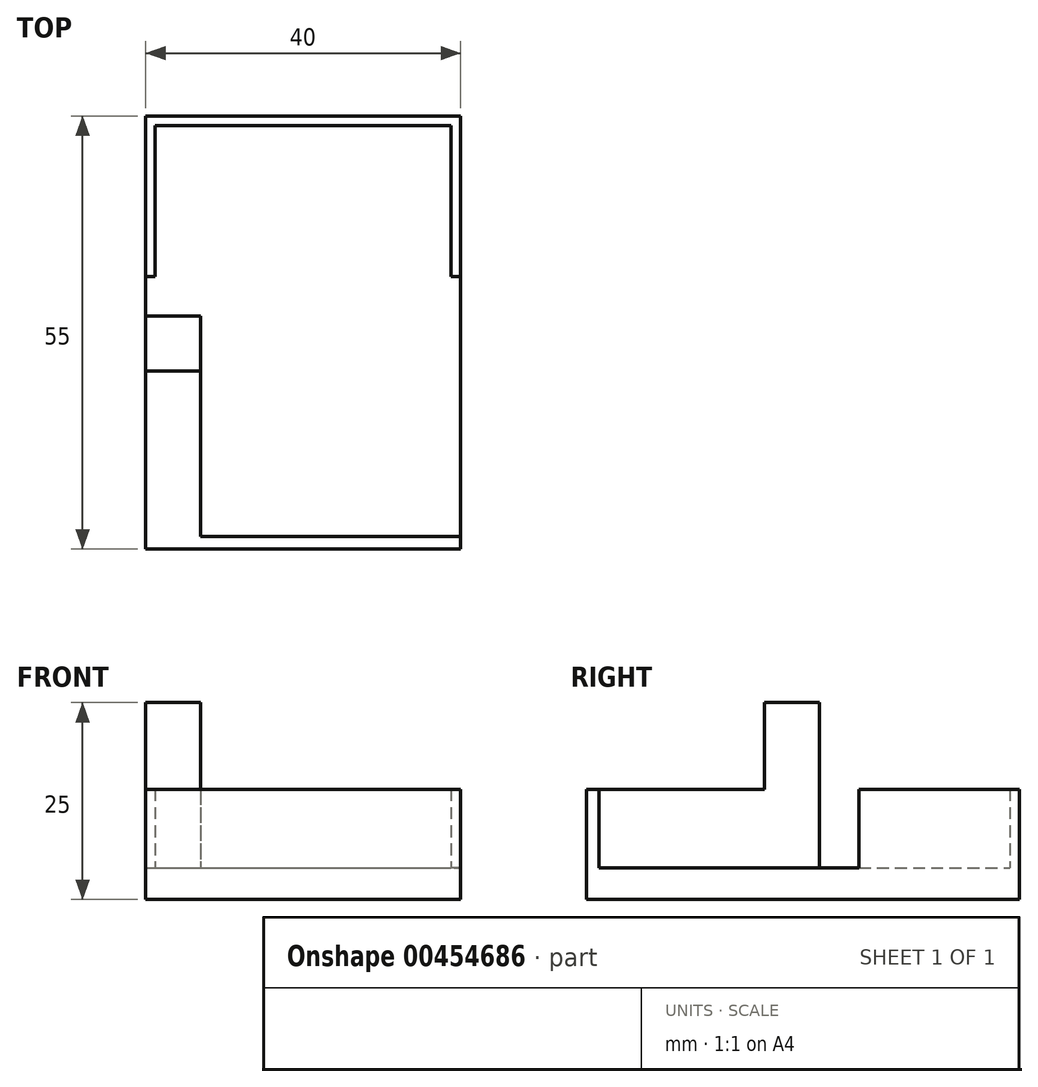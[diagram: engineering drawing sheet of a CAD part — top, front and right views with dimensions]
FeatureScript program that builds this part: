
annotation { "Feature Type Name" : "Feature", "Feature Type Description" : "" }
export const myFeature = defineFeature(function(context is Context, id is Id, definition is map)
    precondition{}
    {
        {
            var Q0;
            Q0=qCreatedBy(makeId("Top.planeOp"),FACE);
            var sketch = newSketch(context, id + "F0", { "sketchPlane" : qUnion([Q0])});
            skLineSegment(sketch, "E0.bottom", {"start": v(0, 0) * mm, "end": v(40, 0) * mm});
            skLineSegment(sketch, "E0.top", {"start": v(0, 55) * mm, "end": v(40, 55) * mm});
            skLineSegment(sketch, "E0.left", {"start": v(0, 0) * mm, "end": v(0, 55) * mm});
            skLineSegment(sketch, "E0.right", {"start": v(40, 0) * mm, "end": v(40, 55) * mm});
            skLineSegment(sketch, "E1.0", {"start": v(7, 1.6) * mm, "end": v(40, 1.6) * mm});
            skLineSegment(sketch, "E2.0", {"start": v(0, 29.6) * mm, "end": v(7, 29.6) * mm});
            skLineSegment(sketch, "E3.0", {"start": v(7, 1.6) * mm, "end": v(7, 29.6) * mm});
            skLineSegment(sketch, "E4.0", {"start": v(0, 34.6) * mm, "end": v(1.2, 34.6) * mm});
            skLineSegment(sketch, "E5.0", {"start": v(1.2, 53.8) * mm, "end": v(38.8, 53.8) * mm});
            skLineSegment(sketch, "E6", {"start": v(40, 34.6) * mm, "end": v(38.8, 34.6) * mm});
            skLineSegment(sketch, "E7", {"start": v(38.8, 34.6) * mm, "end": v(38.8, 53.8) * mm});
            skPoint(sketch, "E8.orphan", {"position": v(7, 34.6) * mm});
            skLineSegment(sketch, "E9.trimOffspring", {"start": v(1.2, 34.6) * mm, "end": v(1.2, 53.8) * mm});
            skPoint(sketch, "E10.orphan", {"position": v(40, 53.8) * mm});
            skLineSegment(sketch, "E11", {"start": v(0, 29.6) * mm, "end": v(0, 22.6) * mm});
            skLineSegment(sketch, "E12", {"start": v(0, 22.6) * mm, "end": v(7, 22.6) * mm});
            skSolve(sketch);
        }
        {
            var Q0;
            {var subQ4=sQuery(id+"F0.wireOp",EDGE,"E1.0");Q0=makeQuery(id+"F0.imprint","IMPRINT",FACE,{"disambiguationData":[TD([[makeQuery(id+"F0.imprint","IMPRINT",EDGE,{"derivedFrom":subQ4}),1.0]])]});}
            extrude(context, id + "F1", {"entities" : qUnion([Q0]), "depth" : 4 * mm});
        }
        {
            var Q0;
            {var subQ2=sQuery(id+"F0.wireOp",EDGE,"E0.bottom");Q0=makeQuery(id+"F0.imprint","IMPRINT",FACE,{"disambiguationData":[TD([[makeQuery(id+"F0.imprint","IMPRINT",EDGE,{"derivedFrom":subQ2}),1.0]])]});}
            var Q1;
            {var subQ1=sQuery(id+"F0.wireOp",EDGE,"E0.top");Q1=makeQuery(id+"F0.imprint","IMPRINT",FACE,{"disambiguationData":[TD([[makeQuery(id+"F0.imprint","IMPRINT",EDGE,{"derivedFrom":subQ1}),-1.0]])]});}
            extrude(context, id + "F2", {"entities" : qUnion([Q0, Q1]), "operationType" : NewBodyOperationType.ADD, "depth" : 14 * mm});
        }
        {
            var Q0;
            {var subQ0=sQuery(id+"F0.wireOp",EDGE,"E2.0");Q0=makeQuery(id+"F0.imprint","IMPRINT",FACE,{"disambiguationData":[TD([[makeQuery(id+"F0.imprint","IMPRINT",EDGE,{"derivedFrom":subQ0}),-1.0]])]});}
            extrude(context, id + "F3", {"entities" : qUnion([Q0]), "operationType" : NewBodyOperationType.ADD, "depth" : 25 * mm});
        }
    });
